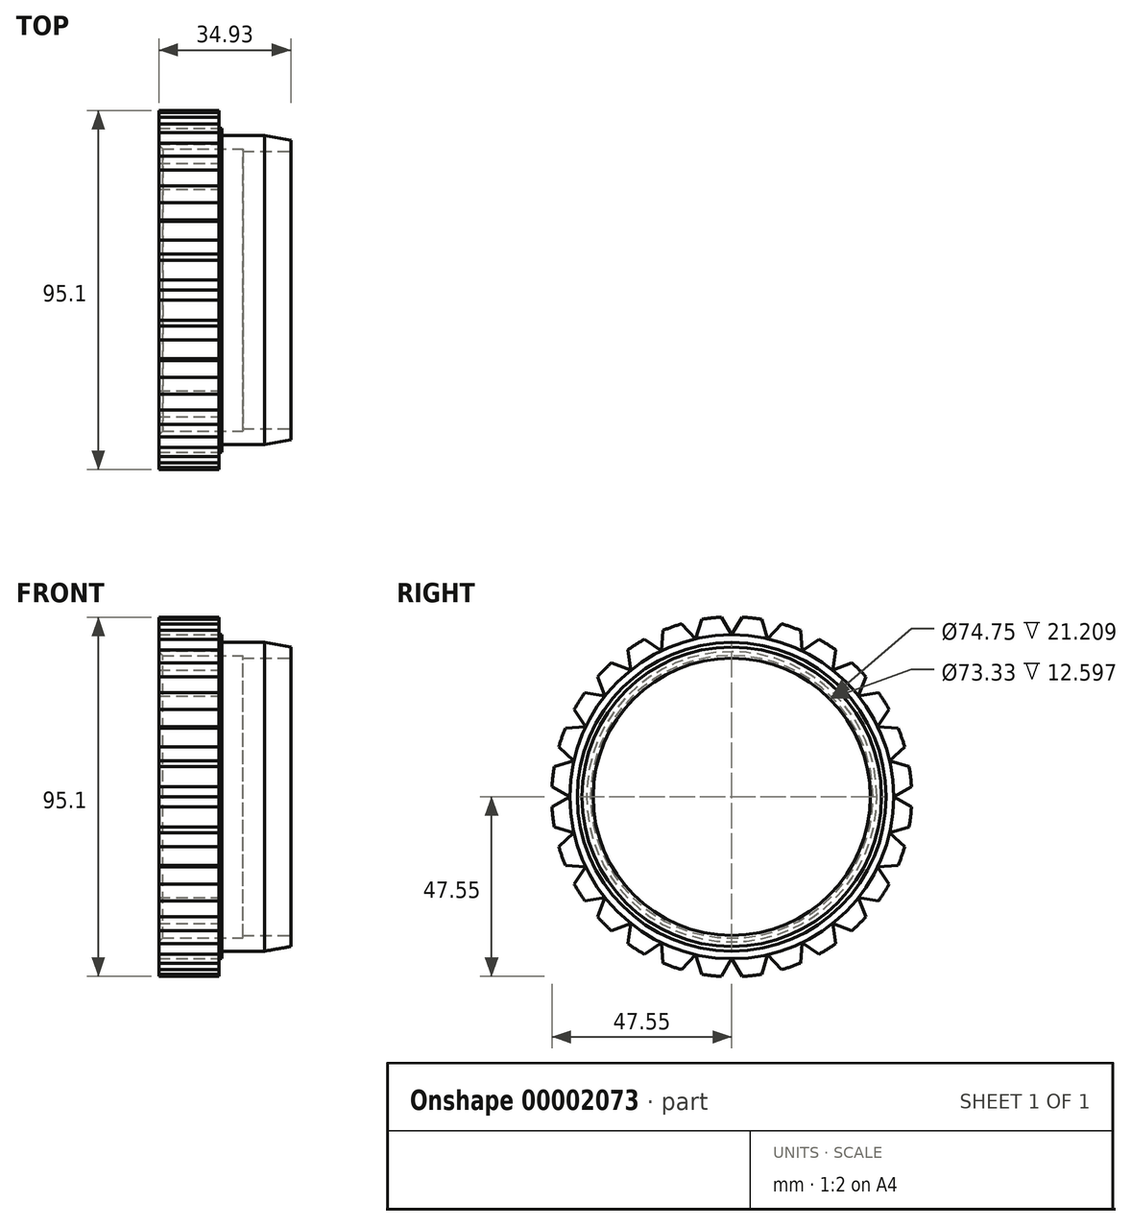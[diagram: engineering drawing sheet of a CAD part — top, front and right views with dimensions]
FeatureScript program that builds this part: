
annotation { "Feature Type Name" : "Feature", "Feature Type Description" : "" }
export const myFeature = defineFeature(function(context is Context, id is Id, definition is map)
    precondition{}
    {
        {
            var Q0;
            Q0=qCreatedBy(makeId("Front.planeOp"),FACE);
            var sketch = newSketch(context, id + "F0", { "sketchPlane" : qUnion([Q0])});
            skLineSegment(sketch, "E0", {"start": v(-34.93, 37.38) * mm, "end": v(-34.93, 47.62) * mm});
            skLineSegment(sketch, "E1", {"start": v(-34.93, 47.63) * mm, "end": v(-19.05, 47.63) * mm});
            skLineSegment(sketch, "E2", {"start": v(-19.05, 47.63) * mm, "end": v(-19.05, 42.86) * mm});
            skLineSegment(sketch, "E3", {"start": v(-19.05, 42.86) * mm, "end": v(-18.26, 42.86) * mm});
            skLineSegment(sketch, "E4", {"start": v(-18.26, 42.86) * mm, "end": v(-18.26, 41.65) * mm});
            skLineSegment(sketch, "E5", {"start": v(-17.46, 40.86) * mm, "end": v(-6.99, 40.86) * mm});
            skLineSegment(sketch, "E6", {"start": v(-6.99, 40.86) * mm, "end": v(0, 39.62) * mm});
            skLineSegment(sketch, "E7", {"start": v(-12.7, 36.66) * mm, "end": v(-0.1, 36.66) * mm});
            skLineSegment(sketch, "E8", {"start": v(0, 39.62) * mm, "end": v(-0.1, 36.66) * mm});
            skPoint(sketch, "E9.orphan", {"position": v(0, 36.66) * mm});
            skLineSegment(sketch, "E10", {"start": v(0, 0) * mm, "end": v(-39.38, 0) * mm, "construction": true});
            skPoint(sketch, "E11.visualSharp", {"position": v(-18.26, 40.86) * mm});
            skArc(sketch, "E11.filletArc", {"start": v(-18.26, 41.65) * mm, "mid": v(-18.02, 41.09) * mm, "end": v(-17.46, 40.86) * mm});
            skLineSegment(sketch, "E12", {"start": v(-34.93, 37.38) * mm, "end": v(-12.7, 37.38) * mm});
            skLineSegment(sketch, "E13", {"start": v(-12.7, 37.38) * mm, "end": v(-12.7, 36.66) * mm});
            skSolve(sketch);
        }
        {
            var Q0;
            Q0 = qSketchRegion(id + "F0", true);
            var Q1;
            Q1=sQuery(id+"F0.wireOp",EDGE,"E10");
            revolve(context, id + "F1", {"entities" : qUnion([Q0]), "axis" : qUnion([Q1]), "revolveType" : RevolveType.FULL});
        }
        {
            var Q0;
            Q0=qCreatedBy(makeId("Right.planeOp"),FACE);
            var sketch = newSketch(context, id + "F2", { "sketchPlane" : qUnion([Q0])});
            skLineSegment(sketch, "E14", {"start": v(0, 0) * mm, "end": v(0, 52.33) * mm, "construction": true});
            skLineSegment(sketch, "E15", {"start": v(0, 42.86) * mm, "end": v(-3.09, 48.21) * mm});
            skCircle(sketch, "E16", {"center": v(0, 0) * mm, "radius": 42.86 * mm, "construction": true});
            skLineSegment(sketch, "E17.0.MirrorCS", {"start": v(0, 42.86) * mm, "end": v(3.09, 48.21) * mm});
            skLineSegment(sketch, "E18", {"start": v(-3.09, 48.21) * mm, "end": v(3.09, 48.21) * mm});
            skSolve(sketch);
        }
        {
            var Q0;
            Q0=makeQuery(id+"F2.imprint","IMPRINT",FACE,{"disambiguationData":[TD([[makeQuery(id+"F2.imprint","IMPRINT",EDGE,{"derivedFrom":sQuery(id+"F2.wireOp",EDGE,"E15")}),-1.0]])]});
            extrude(context, id + "F3", {"entities" : qUnion([Q0]), "operationType" : NewBodyOperationType.REMOVE, "endBound" : BoundingType.THROUGH_ALL, "oppositeDirection" : true, "depth" : 25.4 * mm});
        }
        {
            var Q0;
            Q0=makeQuery(id+"F3.boolean.opBoolean","COPY",FACE,{"derivedFrom":makeQuery(id+"F3.opExtrude","SWEPT_FACE",FACE,{"disambiguationData":[OSD([sQuery(id+"F2.wireOp",EDGE,"E15")])]})});
            var Q1;
            Q1=makeQuery(id+"F3.boolean.opBoolean","COPY",FACE,{"derivedFrom":makeQuery(id+"F3.opExtrude","SWEPT_FACE",FACE,{"disambiguationData":[OSD([sQuery(id+"F2.wireOp",EDGE,"E17.0.MirrorCS")])]})});
            var Q2;
            Q2=makeQuery(id+"F1.opRevolve","SWEPT_BODY",BODY,{"disambiguationData":[OSD([sQuery(id+"F0.wireOp",EDGE,"E0"),sQuery(id+"F0.wireOp",EDGE,"E1"),sQuery(id+"F0.wireOp",EDGE,"E2"),sQuery(id+"F0.wireOp",EDGE,"E3"),sQuery(id+"F0.wireOp",EDGE,"E4"),sQuery(id+"F0.wireOp",EDGE,"E5"),sQuery(id+"F0.wireOp",EDGE,"E6"),sQuery(id+"F0.wireOp",EDGE,"E7"),sQuery(id+"F0.wireOp",EDGE,"E8"),sQuery(id+"F0.wireOp",EDGE,"E11.filletArc"),sQuery(id+"F0.wireOp",EDGE,"E12"),sQuery(id+"F0.wireOp",EDGE,"E13")])]});
            var Q3;
            Q3=makeQuery(id+"F1.opRevolve","SWEPT_EDGE",EDGE,{"disambiguationData":[OSD([sQuery(id+"F0.wireOp",EDGE,"E6"),sQuery(id+"F0.wireOp",EDGE,"E8")])]});
            circularPattern(context, id + "F4", {"faces" : qUnion([Q0, Q1]), "axis" : qUnion([Q3]), "angle" : 360 * degree, "instanceCount" : 28, "equalSpace" : true, "patternType" : PatternType.FACE});
        }
        {
            var Q0;
            Q0=makeQuery(id+"F1.opRevolve","SWEPT_EDGE",EDGE,{"disambiguationData":[OSD([sQuery(id+"F0.wireOp",EDGE,"E0"),sQuery(id+"F0.wireOp",EDGE,"E12")])]});
            chamfer(context, id + "F5", {"entities" : qUnion([Q0]), "width" : 1.02 * mm, "tangentPropagation" : true});
        }
    });
